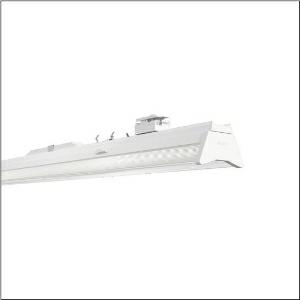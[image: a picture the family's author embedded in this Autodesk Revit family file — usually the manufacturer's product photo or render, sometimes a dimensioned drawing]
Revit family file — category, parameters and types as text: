
# Revit family: licross_21_performance_mo_52tm16cn46xg
name_source: partatom
category: Lighting Fixtures
units: mm (PartAtom-declared; Revit-internal decimal feet)

## family parameters
Cut with Voids When Loaded = No
Host = Face
Light Source = No
Part Type = Normal
Room Calculation Point = No
Round Connector Dimension = Use Diameter
Shared = No

## types (1)
- --- (1 x LED, 6000 lm, 32 W, 4000K)
    Apparent Load = 32 VA
    CIE Flux Codes = 66 88 96 79 100
    Color Rendering = 80
    Color Temperature = 4000K
    Default Elevation = 1800 mm
    Description = Licross 21 Performance MO, luminaire insert, of sheet steel, galvanised, coil coated, white, length: 1.500mm, width: 120mm, height: 123mm, LED rated luminous flux: 6.000lm, light colour: 840, SDCM (Standard Deviation of Colour Matching)MacAdam ≤ 3 SDCM (initial), control gear: ON/OFF Multilumen, CLOi, with plug, 3-pole, with phase selection, mains connection: 220..240V, AC, 50/60Hz, start of lifetime: 32W, end of service life: 38W, internal wiring halogen-free, primary light control with lens, of plastic, primary optical cover: cover, of PMMA, light emission: direct/indirect distribution, primary light characteristic: symmetric, protection rating (complete): IP40, insulation class (complete): insulation class I (protective earthing), certification: CE, ENEC, UKCA, protection symbol: D if used in an environment without relevant dust loads with corresponding accessories, impact resistance: IK06, permissible ambient temperature for indoor applications: -35..+55°C, corresponds to IFS (International Featured Standards) requirements for safety and quality in the food industry, reducing of maximum allowable ambient temperature of 5°C with ceiling mounting, LABS conformity tested according to VDMA 24364:2018-05, The light source and the operating device comply with the requirements of the Ecodesign Regulation (EU) 2019/2020 and are replaceable in accordance with this regulation, packaging unit: 1 piece
    Height = 114 mm
    Lamp = 1 x LED
    Lamp Light Flux = 6000 lm
    Lamp Power = 32 W
    Lamp count = 1
    Length = 1500 mm
    Luminous efficacy = 188 lm/W
    Manufacturer = Siteco
    ModVariant = No
    Model = 52TM16CN46XG
    Mounting Place = Ceiling
    Mounting Type = Pendant
    Number of Poles = 1
    OnlyDefault = Yes
    Power Factor = 1
    Product Name = Licross 21 Performance MO
    Product group = luminaire insert | ceiling pendant
    ProductGroupID = 901
    Protection Class = Protection class I
    Protection Degree = IP 40
    RLX_Detail_Level = 1
    RLX_Emergency_Light_Flux = 0 lm
    RLX_Emergency_Type = 0
    RLX_Emergency_Type_DB = No
    RlxData = <blob elided: 32025 chars, md5=1bdae002>
    Socket = socket
    Standby Power = 0 W
    System Light Flux = 6000 lm
    System Power = 32 W
    Type Comments = factory setting: luminous flux: 100 % | (A | C | E) | 74 mA
    Type Image = l_1256138.jpg
    URL = http://relux.com
    VarID = @adj_111529
    Voltage = 0 V
    Weight = 0.00 kg
    Width = 120 mm

## geometry (parser evidence)
native form markers: Blend x4, Sweep x11
no freeform markers — native parametric forms only
